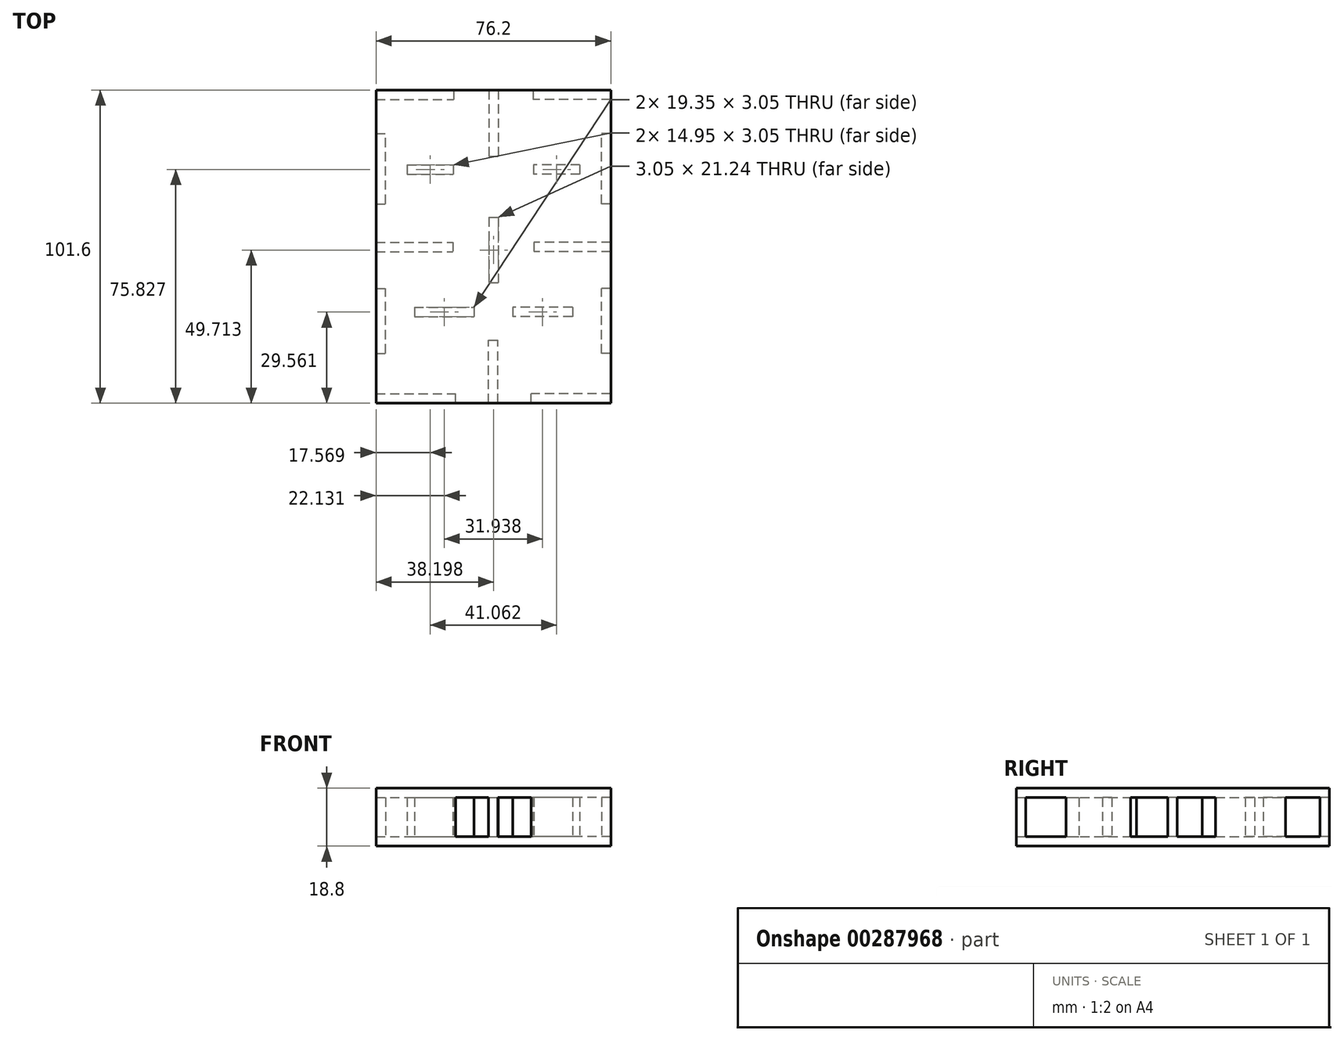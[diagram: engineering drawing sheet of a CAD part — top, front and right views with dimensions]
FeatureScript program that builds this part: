
annotation { "Feature Type Name" : "Feature", "Feature Type Description" : "" }
export const myFeature = defineFeature(function(context is Context, id is Id, definition is map)
    precondition{}
    {
        {
            var Q0;
            Q0=qCreatedBy(makeId("Top.planeOp"),FACE);
            var sketch = newSketch(context, id + "F0", { "sketchPlane" : qUnion([Q0])});
            skLineSegment(sketch, "E0.bottom", {"start": v(-38.1, 50.8) * mm, "end": v(38.1, 50.8) * mm});
            skLineSegment(sketch, "E0.top", {"start": v(-38.1, -50.8) * mm, "end": v(38.1, -50.8) * mm});
            skLineSegment(sketch, "E0.left", {"start": v(-38.1, 50.8) * mm, "end": v(-38.1, -50.8) * mm});
            skLineSegment(sketch, "E0.right", {"start": v(38.1, 50.8) * mm, "end": v(38.1, -50.8) * mm});
            skPoint(sketch, "E0.middle", {"position": v(0, 0) * mm});
            skSolve(sketch);
        }
        {
            var Q0;
            Q0=makeQuery(id+"F0.imprint","IMPRINT",FACE,{"disambiguationData":[TD([[makeQuery(id+"F0.imprint","IMPRINT",EDGE,{"derivedFrom":sQuery(id+"F0.wireOp",EDGE,"E0.bottom")}),-1.0]])]});
            extrude(context, id + "F1", {"entities" : qUnion([Q0]), "depth" : 3.05 * mm});
        }
        {
            var Q0;
            Q0=makeQuery(id+"F1.opExtrude","CAP_FACE",FACE,{"disambiguationData":[OSD([sQuery(id+"F0.wireOp",EDGE,"E0.bottom"),sQuery(id+"F0.wireOp",EDGE,"E0.top"),sQuery(id+"F0.wireOp",EDGE,"E0.left"),sQuery(id+"F0.wireOp",EDGE,"E0.right")])],"isStart":false});
            var sketch = newSketch(context, id + "F2", { "sketchPlane" : qUnion([Q0])});
            skLineSegment(sketch, "E1.bottom", {"start": v(-38.1, 50.8) * mm, "end": v(-12.86, 50.8) * mm});
            skLineSegment(sketch, "E1.top", {"start": v(-38.1, 47.75) * mm, "end": v(-12.86, 47.75) * mm});
            skLineSegment(sketch, "E1.left", {"start": v(-38.1, 50.8) * mm, "end": v(-38.1, 47.75) * mm});
            skLineSegment(sketch, "E1.right", {"start": v(-12.86, 50.8) * mm, "end": v(-12.86, 47.75) * mm});
            skLineSegment(sketch, "E2.bottom", {"start": v(-38.1, 1.46) * mm, "end": v(-13.17, 1.46) * mm});
            skLineSegment(sketch, "E2.top", {"start": v(-38.1, -1.59) * mm, "end": v(-13.17, -1.59) * mm});
            skLineSegment(sketch, "E2.left", {"start": v(-38.1, 1.46) * mm, "end": v(-38.1, -1.59) * mm});
            skLineSegment(sketch, "E2.right", {"start": v(-13.17, 1.46) * mm, "end": v(-13.17, -1.59) * mm});
            skLineSegment(sketch, "E3.bottom", {"start": v(-38.1, -50.8) * mm, "end": v(-12.3, -50.8) * mm});
            skLineSegment(sketch, "E3.top", {"start": v(-38.1, -47.75) * mm, "end": v(-12.3, -47.75) * mm});
            skLineSegment(sketch, "E3.left", {"start": v(-38.1, -50.8) * mm, "end": v(-38.1, -47.75) * mm});
            skLineSegment(sketch, "E3.right", {"start": v(-12.3, -50.8) * mm, "end": v(-12.3, -47.75) * mm});
            skLineSegment(sketch, "E4.bottom", {"start": v(-38.1, -34.64) * mm, "end": v(-35.05, -34.64) * mm});
            skLineSegment(sketch, "E4.top", {"start": v(-38.1, -13.61) * mm, "end": v(-35.05, -13.61) * mm});
            skLineSegment(sketch, "E4.left", {"start": v(-38.1, -34.64) * mm, "end": v(-38.1, -13.61) * mm});
            skLineSegment(sketch, "E4.right", {"start": v(-35.05, -34.64) * mm, "end": v(-35.05, -13.61) * mm});
            skLineSegment(sketch, "E5.bottom", {"start": v(-38.1, 13.9) * mm, "end": v(-35.05, 13.9) * mm});
            skLineSegment(sketch, "E5.top", {"start": v(-38.1, 36.69) * mm, "end": v(-35.05, 36.69) * mm});
            skLineSegment(sketch, "E5.left", {"start": v(-38.1, 13.9) * mm, "end": v(-38.1, 36.69) * mm});
            skLineSegment(sketch, "E5.right", {"start": v(-35.05, 13.9) * mm, "end": v(-35.05, 36.69) * mm});
            skLineSegment(sketch, "E6.bottom", {"start": v(-28, 26.55) * mm, "end": v(-13.06, 26.55) * mm});
            skLineSegment(sketch, "E6.top", {"start": v(-28, 23.5) * mm, "end": v(-13.06, 23.5) * mm});
            skLineSegment(sketch, "E6.left", {"start": v(-28, 26.55) * mm, "end": v(-28, 23.5) * mm});
            skLineSegment(sketch, "E6.right", {"start": v(-13.06, 26.55) * mm, "end": v(-13.06, 23.5) * mm});
            skLineSegment(sketch, "E7.bottom", {"start": v(-1.45, 50.8) * mm, "end": v(1.6, 50.8) * mm});
            skLineSegment(sketch, "E7.top", {"start": v(-1.45, 29.35) * mm, "end": v(1.6, 29.35) * mm});
            skLineSegment(sketch, "E7.left", {"start": v(-1.45, 50.8) * mm, "end": v(-1.45, 29.35) * mm});
            skLineSegment(sketch, "E7.right", {"start": v(1.6, 50.8) * mm, "end": v(1.6, 29.35) * mm});
            skLineSegment(sketch, "E8.bottom", {"start": v(-1.43, 9.53) * mm, "end": v(1.62, 9.53) * mm});
            skLineSegment(sketch, "E8.top", {"start": v(-1.43, -11.7) * mm, "end": v(1.62, -11.7) * mm});
            skLineSegment(sketch, "E8.left", {"start": v(-1.43, 9.53) * mm, "end": v(-1.43, -11.7) * mm});
            skLineSegment(sketch, "E8.right", {"start": v(1.62, 9.53) * mm, "end": v(1.62, -11.7) * mm});
            skLineSegment(sketch, "E9.bottom", {"start": v(-1.6, -50.8) * mm, "end": v(1.45, -50.8) * mm});
            skLineSegment(sketch, "E9.top", {"start": v(-1.6, -30.38) * mm, "end": v(1.45, -30.38) * mm});
            skLineSegment(sketch, "E9.left", {"start": v(-1.6, -50.8) * mm, "end": v(-1.6, -30.38) * mm});
            skLineSegment(sketch, "E9.right", {"start": v(1.45, -50.8) * mm, "end": v(1.45, -30.38) * mm});
            skLineSegment(sketch, "E10.bottom", {"start": v(-25.65, -19.72) * mm, "end": v(-6.3, -19.72) * mm});
            skLineSegment(sketch, "E10.top", {"start": v(-25.65, -22.76) * mm, "end": v(-6.3, -22.76) * mm});
            skLineSegment(sketch, "E10.left", {"start": v(-25.65, -19.72) * mm, "end": v(-25.65, -22.76) * mm});
            skLineSegment(sketch, "E10.right", {"start": v(-6.3, -19.72) * mm, "end": v(-6.3, -22.76) * mm});
            skLineSegment(sketch, "E11.MirrorCS", {"start": v(38.1, 50.8) * mm, "end": v(12.86, 50.8) * mm});
            skLineSegment(sketch, "E12.MirrorCS", {"start": v(12.86, 50.8) * mm, "end": v(12.86, 47.75) * mm});
            skLineSegment(sketch, "E13.MirrorCS", {"start": v(38.1, 47.75) * mm, "end": v(12.86, 47.75) * mm});
            skLineSegment(sketch, "E14.MirrorCS", {"start": v(38.1, 50.8) * mm, "end": v(38.1, 47.75) * mm});
            skLineSegment(sketch, "E15.MirrorCS", {"start": v(38.1, 36.69) * mm, "end": v(35.05, 36.69) * mm});
            skLineSegment(sketch, "E16.MirrorCS", {"start": v(35.05, 13.9) * mm, "end": v(35.05, 36.69) * mm});
            skLineSegment(sketch, "E17.MirrorCS", {"start": v(38.1, 13.9) * mm, "end": v(38.1, 36.69) * mm});
            skLineSegment(sketch, "E18.MirrorCS", {"start": v(38.1, 13.9) * mm, "end": v(35.05, 13.9) * mm});
            skLineSegment(sketch, "E19.MirrorCS", {"start": v(28, 26.55) * mm, "end": v(28, 23.5) * mm});
            skLineSegment(sketch, "E20.MirrorCS", {"start": v(28, 26.55) * mm, "end": v(13.06, 26.55) * mm});
            skLineSegment(sketch, "E21.MirrorCS", {"start": v(13.06, 26.55) * mm, "end": v(13.06, 23.5) * mm});
            skLineSegment(sketch, "E22.MirrorCS", {"start": v(28, 23.5) * mm, "end": v(13.06, 23.5) * mm});
            skLineSegment(sketch, "E23.MirrorCS", {"start": v(38.1, 1.46) * mm, "end": v(13.17, 1.46) * mm});
            skLineSegment(sketch, "E24.MirrorCS", {"start": v(38.1, 1.46) * mm, "end": v(38.1, -1.59) * mm});
            skLineSegment(sketch, "E25.MirrorCS", {"start": v(38.1, -1.59) * mm, "end": v(13.17, -1.59) * mm});
            skLineSegment(sketch, "E26.MirrorCS", {"start": v(13.17, 1.46) * mm, "end": v(13.17, -1.59) * mm});
            skLineSegment(sketch, "E27.MirrorCS", {"start": v(25.65, -19.72) * mm, "end": v(6.3, -19.72) * mm});
            skLineSegment(sketch, "E28.MirrorCS", {"start": v(25.65, -19.72) * mm, "end": v(25.65, -22.76) * mm});
            skLineSegment(sketch, "E29.MirrorCS", {"start": v(25.65, -22.76) * mm, "end": v(6.3, -22.76) * mm});
            skLineSegment(sketch, "E30.MirrorCS", {"start": v(6.3, -19.72) * mm, "end": v(6.3, -22.76) * mm});
            skLineSegment(sketch, "E31.MirrorCS", {"start": v(38.1, -13.61) * mm, "end": v(35.05, -13.61) * mm});
            skLineSegment(sketch, "E32.MirrorCS", {"start": v(38.1, -34.64) * mm, "end": v(38.1, -13.61) * mm});
            skLineSegment(sketch, "E33.MirrorCS", {"start": v(35.05, -34.64) * mm, "end": v(35.05, -13.61) * mm});
            skLineSegment(sketch, "E34.MirrorCS", {"start": v(38.1, -34.64) * mm, "end": v(35.05, -34.64) * mm});
            skLineSegment(sketch, "E35.MirrorCS", {"start": v(12.3, -50.8) * mm, "end": v(12.3, -47.75) * mm});
            skLineSegment(sketch, "E36.MirrorCS", {"start": v(38.1, -47.75) * mm, "end": v(12.3, -47.75) * mm});
            skLineSegment(sketch, "E37.MirrorCS", {"start": v(38.1, -50.8) * mm, "end": v(38.1, -47.75) * mm});
            skLineSegment(sketch, "E38.MirrorCS", {"start": v(38.1, -50.8) * mm, "end": v(12.3, -50.8) * mm});
            skSolve(sketch);
        }
        {
            var Q0;
            Q0=makeQuery(id+"F2.imprint","IMPRINT",FACE,{"disambiguationData":[TD([[makeQuery(id+"F2.imprint","IMPRINT",EDGE,{"derivedFrom":sQuery(id+"F2.wireOp",EDGE,"E1.bottom")}),-1.0]])]});
            var Q1;
            Q1=makeQuery(id+"F2.imprint","IMPRINT",FACE,{"disambiguationData":[TD([[makeQuery(id+"F2.imprint","IMPRINT",EDGE,{"derivedFrom":sQuery(id+"F2.wireOp",EDGE,"E11.MirrorCS")}),-1.0]])]});
            var Q2;
            Q2=makeQuery(id+"F2.imprint","IMPRINT",FACE,{"disambiguationData":[TD([[makeQuery(id+"F2.imprint","IMPRINT",EDGE,{"derivedFrom":sQuery(id+"F2.wireOp",EDGE,"E7.bottom")}),-1.0]])]});
            var Q3;
            Q3=makeQuery(id+"F2.imprint","IMPRINT",FACE,{"disambiguationData":[TD([[makeQuery(id+"F2.imprint","IMPRINT",EDGE,{"derivedFrom":sQuery(id+"F2.wireOp",EDGE,"E6.bottom")}),-1.0]])]});
            var Q4;
            Q4=makeQuery(id+"F2.imprint","IMPRINT",FACE,{"disambiguationData":[TD([[makeQuery(id+"F2.imprint","IMPRINT",EDGE,{"derivedFrom":sQuery(id+"F2.wireOp",EDGE,"E5.bottom")}),1.0]])]});
            var Q5;
            Q5=makeQuery(id+"F2.imprint","IMPRINT",FACE,{"disambiguationData":[TD([[makeQuery(id+"F2.imprint","IMPRINT",EDGE,{"derivedFrom":sQuery(id+"F2.wireOp",EDGE,"E19.MirrorCS")}),-1.0]])]});
            var Q6;
            Q6=makeQuery(id+"F2.imprint","IMPRINT",FACE,{"disambiguationData":[TD([[makeQuery(id+"F2.imprint","IMPRINT",EDGE,{"derivedFrom":sQuery(id+"F2.wireOp",EDGE,"E15.MirrorCS")}),1.0]])]});
            var Q7;
            Q7=makeQuery(id+"F2.imprint","IMPRINT",FACE,{"disambiguationData":[TD([[makeQuery(id+"F2.imprint","IMPRINT",EDGE,{"derivedFrom":sQuery(id+"F2.wireOp",EDGE,"E23.MirrorCS")}),1.0]])]});
            var Q8;
            Q8=makeQuery(id+"F2.imprint","IMPRINT",FACE,{"disambiguationData":[TD([[makeQuery(id+"F2.imprint","IMPRINT",EDGE,{"derivedFrom":sQuery(id+"F2.wireOp",EDGE,"E8.bottom")}),-1.0]])]});
            var Q9;
            Q9=makeQuery(id+"F2.imprint","IMPRINT",FACE,{"disambiguationData":[TD([[makeQuery(id+"F2.imprint","IMPRINT",EDGE,{"derivedFrom":sQuery(id+"F2.wireOp",EDGE,"E2.bottom")}),-1.0]])]});
            var Q10;
            Q10=makeQuery(id+"F2.imprint","IMPRINT",FACE,{"disambiguationData":[TD([[makeQuery(id+"F2.imprint","IMPRINT",EDGE,{"derivedFrom":sQuery(id+"F2.wireOp",EDGE,"E4.bottom")}),1.0]])]});
            var Q11;
            Q11=makeQuery(id+"F2.imprint","IMPRINT",FACE,{"disambiguationData":[TD([[makeQuery(id+"F2.imprint","IMPRINT",EDGE,{"derivedFrom":sQuery(id+"F2.wireOp",EDGE,"E10.bottom")}),-1.0]])]});
            var Q12;
            Q12=makeQuery(id+"F2.imprint","IMPRINT",FACE,{"disambiguationData":[TD([[makeQuery(id+"F2.imprint","IMPRINT",EDGE,{"derivedFrom":sQuery(id+"F2.wireOp",EDGE,"E27.MirrorCS")}),1.0]])]});
            var Q13;
            Q13=makeQuery(id+"F2.imprint","IMPRINT",FACE,{"disambiguationData":[TD([[makeQuery(id+"F2.imprint","IMPRINT",EDGE,{"derivedFrom":sQuery(id+"F2.wireOp",EDGE,"E31.MirrorCS")}),1.0]])]});
            var Q14;
            Q14=makeQuery(id+"F2.imprint","IMPRINT",FACE,{"disambiguationData":[TD([[makeQuery(id+"F2.imprint","IMPRINT",EDGE,{"derivedFrom":sQuery(id+"F2.wireOp",EDGE,"E9.bottom")}),1.0]])]});
            var Q15;
            Q15=makeQuery(id+"F2.imprint","IMPRINT",FACE,{"disambiguationData":[TD([[makeQuery(id+"F2.imprint","IMPRINT",EDGE,{"derivedFrom":sQuery(id+"F2.wireOp",EDGE,"E3.bottom")}),1.0]])]});
            var Q16;
            Q16=makeQuery(id+"F2.imprint","IMPRINT",FACE,{"disambiguationData":[TD([[makeQuery(id+"F2.imprint","IMPRINT",EDGE,{"derivedFrom":sQuery(id+"F2.wireOp",EDGE,"E35.MirrorCS")}),-1.0]])]});
            extrude(context, id + "F3", {"entities" : qUnion([Q0, Q1, Q2, Q3, Q4, Q5, Q6, Q7, Q8, Q9, Q10, Q11, Q12, Q13, Q14, Q15, Q16]), "operationType" : NewBodyOperationType.ADD, "depth" : 12.7 * mm});
        }
        {
            var Q0;
            Q0=makeQuery(id+"F3.opExtrude","CAP_FACE",FACE,{"disambiguationData":[OSD([sQuery(id+"F2.wireOp",EDGE,"E1.bottom"),sQuery(id+"F2.wireOp",EDGE,"E1.top"),sQuery(id+"F2.wireOp",EDGE,"E1.left"),sQuery(id+"F2.wireOp",EDGE,"E1.right")])],"isStart":false});
            var sketch = newSketch(context, id + "F4", { "sketchPlane" : qUnion([Q0])});
            skLineSegment(sketch, "E39.bottom", {"start": v(-38.1, 50.8) * mm, "end": v(38.1, 50.8) * mm});
            skLineSegment(sketch, "E39.top", {"start": v(-38.1, -50.8) * mm, "end": v(38.1, -50.8) * mm});
            skLineSegment(sketch, "E39.left", {"start": v(-38.1, 50.8) * mm, "end": v(-38.1, -50.8) * mm});
            skLineSegment(sketch, "E39.right", {"start": v(38.1, 50.8) * mm, "end": v(38.1, -50.8) * mm});
            skSolve(sketch);
        }
        {
            var Q0;
            {var subQ3=sQuery(id+"F4.wireOp",EDGE,"E39.top");Q0=makeQuery(id+"F4.imprint","IMPRINT",FACE,{"disambiguationData":[TD([[makeQuery(id+"F4.imprint","IMPRINT",EDGE,{"derivedFrom":subQ3}),1.0]])]});}
            var Q1;
            {var subQ4=makeQuery(id+"F3.opExtrude","CAP_EDGE",EDGE,{"disambiguationData":[OSD([sQuery(id+"F2.wireOp",EDGE,"E1.top")])],"isStart":false});Q1=makeQuery(id+"F4.imprint","IMPRINT",FACE,{"disambiguationData":[TD([[makeQuery(id+"F4.imprint","IMPRINT",EDGE,{"derivedFrom":subQ4}),1.0]])]});}
            extrude(context, id + "F5", {"entities" : qUnion([Q0, Q1]), "operationType" : NewBodyOperationType.ADD, "depth" : 3.05 * mm});
        }
    });
